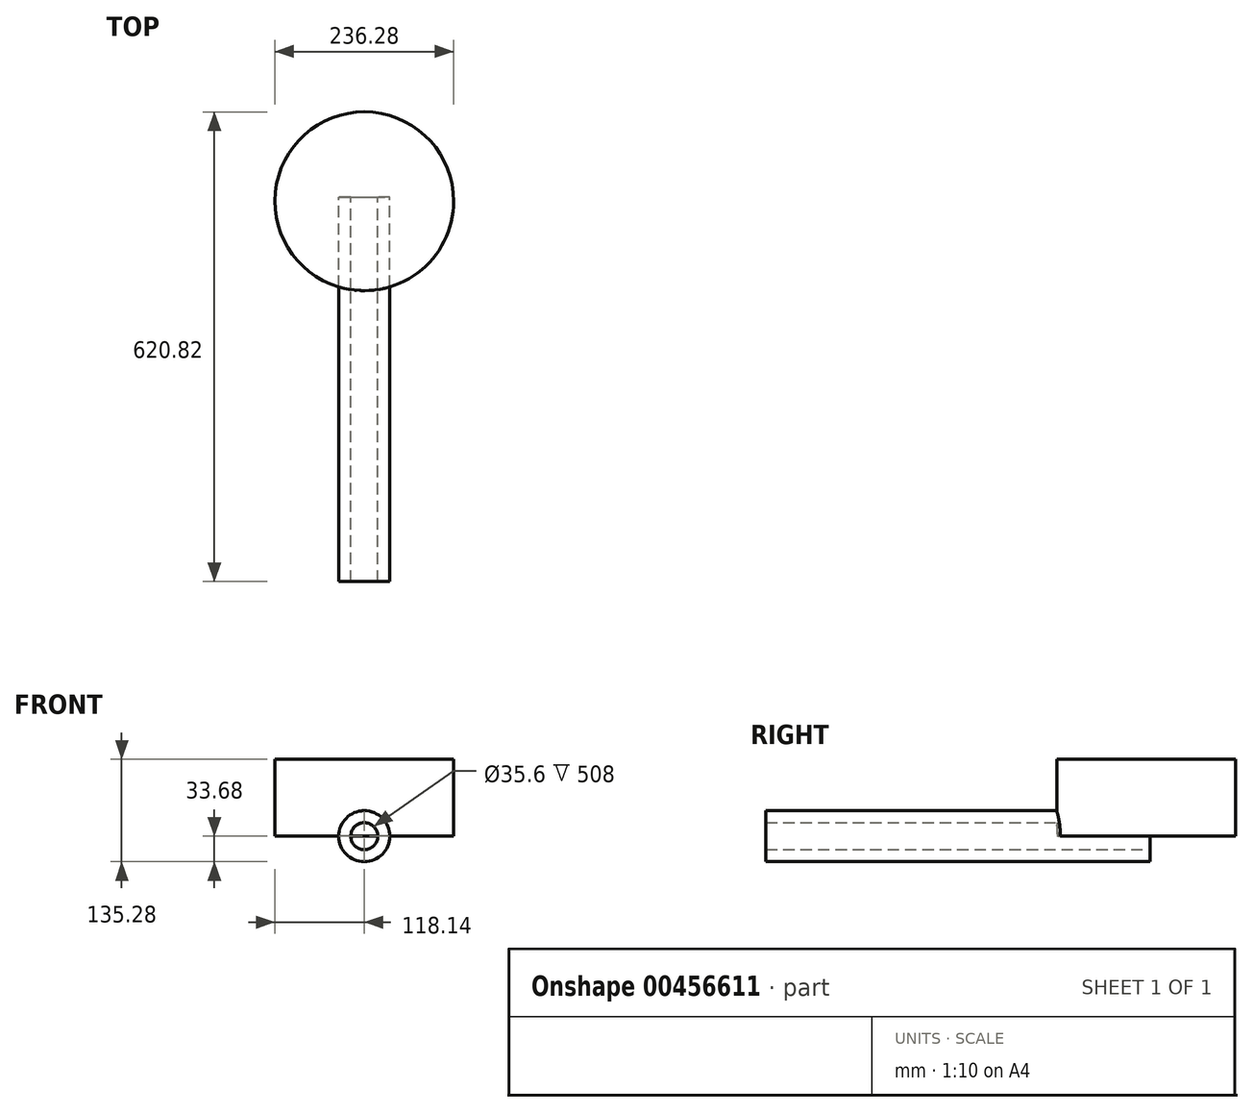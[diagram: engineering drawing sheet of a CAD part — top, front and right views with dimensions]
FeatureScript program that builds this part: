
annotation { "Feature Type Name" : "Feature", "Feature Type Description" : "" }
export const myFeature = defineFeature(function(context is Context, id is Id, definition is map)
    precondition{}
    {
        {
            var Q0;
            Q0=qCreatedBy(makeId("Front.planeOp"),FACE);
            var sketch = newSketch(context, id + "F0", { "sketchPlane" : qUnion([Q0])});
            skCircle(sketch, "E0", {"center": v(0, 0) * mm, "radius": 17.8 * mm});
            skCircle(sketch, "E1", {"center": v(0, 0) * mm, "radius": 33.68 * mm});
            skSolve(sketch);
        }
        {
            var Q0;
            Q0=makeQuery(id+"F0.imprint","IMPRINT",FACE,{"disambiguationData":[TD([[makeQuery(id+"F0.imprint","IMPRINT",EDGE,{"derivedFrom":sQuery(id+"F0.wireOp",EDGE,"E0")}),-1.0]])]});
            extrude(context, id + "F1", {"entities" : qUnion([Q0]), "depth" : 508 * mm});
        }
        {
            var Q0;
            Q0=qCreatedBy(makeId("Top.planeOp"),FACE);
            var sketch = newSketch(context, id + "F2", { "sketchPlane" : qUnion([Q0])});
            skCircle(sketch, "E2", {"center": v(0, -5.32) * mm, "radius": 118.14 * mm});
            skSolve(sketch);
        }
        {
            var Q0;
            Q0=makeQuery(id+"F2.imprint","IMPRINT",FACE,{"disambiguationData":[TD([[makeQuery(id+"F2.imprint","IMPRINT",EDGE,{"derivedFrom":sQuery(id+"F2.wireOp",EDGE,"E2")}),1.0]])]});
            extrude(context, id + "F3", {"entities" : qUnion([Q0]), "operationType" : NewBodyOperationType.ADD, "depth" : 101.6 * mm});
        }
        {
            var Q0;
            Q0=sQuery(id+"F2.wireOp",EDGE,"E2");
            extrude(context, id + "F4", {"bodyType" : ToolBodyType.SURFACE, "surfaceEntities" : qUnion([Q0]), "oppositeDirection" : true, "depth" : 101.6 * mm});
        }
    });
